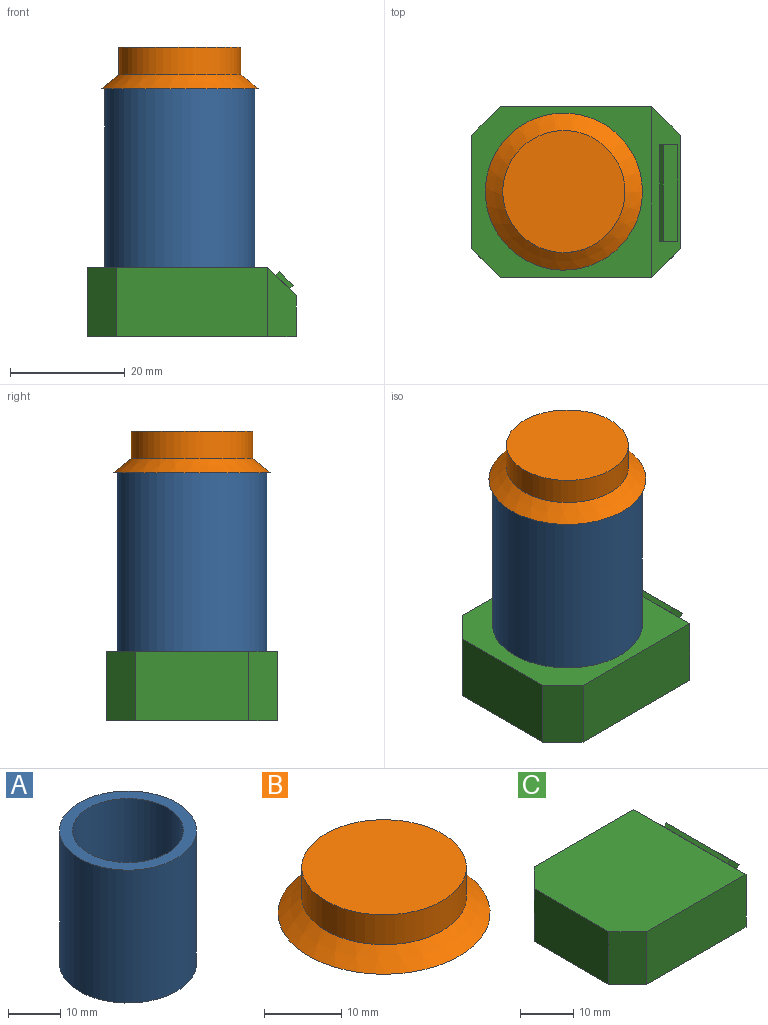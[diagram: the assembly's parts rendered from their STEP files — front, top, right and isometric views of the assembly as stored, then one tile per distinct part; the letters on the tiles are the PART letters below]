
ASSEMBLY  parts=3 mates=2
PART A: 5 faces, bbox 26.2x26.2x31.1 mm
  f0: cylinder r=13.08mm len=31.06mm, axis (0,0,-1), area 2552.9mm2, adj f1,f2
  f1: plane 26.16x26.16mm, normal (0,0,-1), area 537.4mm2, adj f0
  f2: plane 26.16x26.16mm, normal (0,0,1), area 185.8mm2, adj f0,f3
  f3: cylinder r=10.58mm len=28.56mm, axis (0,0,-1), area 1898.8mm2, adj f2,f4
  f4: plane 21.16x21.16mm, normal (0,0,1), area 351.6mm2, adj f3
PART B: 4 faces, bbox 27.4x27.4x7.2 mm
  f0: cone r=13.7mm half-angle=50.5deg, axis (0,0,-1), area 302.7mm2, adj f1,f3
  f1: plane 27.39x27.39mm, normal (0,0,-1), area 589.3mm2, adj f0
  f2: plane 21.28x21.28mm, normal (0,0,1), area 355.5mm2, adj f3
  f3: cylinder r=10.64mm len=21.28mm, axis (0,0,1), area 315.5mm2, adj f0,f2
PART C: 16 faces, bbox 36.3x29.8x12.1 mm
  f0: plane 26.34x12.1mm, normal (0,1,0), area 318.8mm2, adj f4,f5,f6,f9
  f1: plane 19.8x12.1mm, normal (-1,0,0), area 239.6mm2, adj f4,f5,f7,f9
  f2: plane 26.34x12.1mm, normal (0,-1,0), area 318.8mm2, adj f4,f5,f7,f8
  f3: plane 19.8x7.1mm, normal (1,0,0), area 140.6mm2, adj f5,f6,f8,f10
  f4: plane 31.34x29.8mm, normal (0,0,1), area 909.1mm2, adj f0,f1,f2,f7,f9,f10
  f5: plane 36.34x29.8mm, normal (0,0,-1), area 1033.1mm2, adj f0,f1,f2,f3,f6,f7,f8,f9
  f6: plane 12.1x5mm, normal (0.71,0.71,0), area 67.9mm2, adj f0,f3,f5,f10
  f7: plane 12.1x5mm, normal (-0.71,-0.71,0), area 85.6mm2, adj f1,f2,f4,f5
  f8: plane 12.1x5mm, normal (0.71,-0.71,0), area 67.9mm2, adj f2,f3,f5,f10
  f9: plane 12.1x5mm, normal (-0.71,0.71,0), area 85.6mm2, adj f0,f1,f4,f5
  f10: plane 29.8x5mm, normal (0.71,0,0.71), area 117.5mm2, adj f3,f4,f6,f8,f11,f12,f13,f14
  f11: plane 16.82x0.64mm, normal (-0.71,0,0.71), area 15.3mm2, adj f10,f12,f14,f15
  f12: plane 3.08x3.08mm, normal (0,-1,0), area 3.1mm2, adj f10,f11,f13,f15
  f13: plane 16.82x0.64mm, normal (0.71,0,-0.71), area 15.3mm2, adj f10,f12,f14,f15
  f14: plane 3.08x3.08mm, normal (0,1,0), area 3.1mm2, adj f10,f11,f13,f15
  f15: plane 16.82x2.43mm, normal (0.71,0,0.71), area 57.9mm2, adj f11,f12,f13,f14
PLACE A t=(27.87,24.47,-4.3)mm
PLACE B t=(27.87,24.47,-6.77)mm
PLACE C t=(-24.05,-14.72,0.36)mm fixed
MATE fastened C.f4 <-> A.f0  axis (0,0,1) through (27.87,24.47,12.46)mm
MATE fastened B.f0 <-> A.f0  axis (0,0,-1) through (27.87,24.47,43.52)mm
